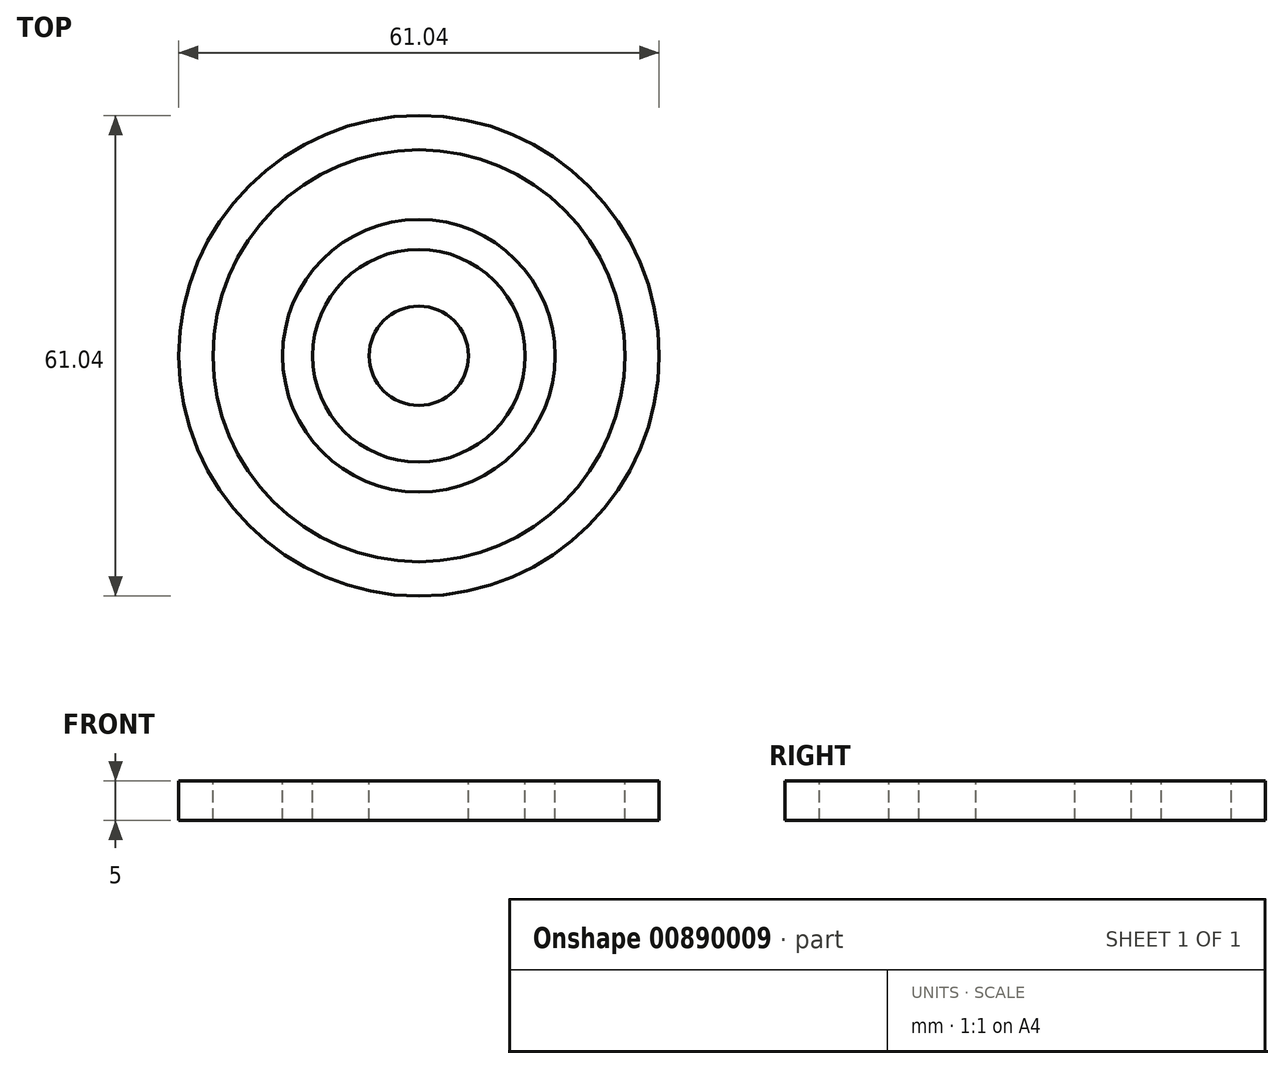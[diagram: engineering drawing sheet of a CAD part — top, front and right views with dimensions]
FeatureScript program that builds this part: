
annotation { "Feature Type Name" : "Feature", "Feature Type Description" : "" }
export const myFeature = defineFeature(function(context is Context, id is Id, definition is map)
    precondition{}
    {
        {
            var Q0;
            Q0=qCreatedBy(makeId("Top.planeOp"),FACE);
            var sketch = newSketch(context, id + "F0", { "sketchPlane" : qUnion([Q0])});
            skCircle(sketch, "E0", {"center": v(0, 0) * mm, "radius": 30.52 * mm});
            skCircle(sketch, "E1", {"center": v(0, 0) * mm, "radius": 26.17 * mm});
            skCircle(sketch, "E2", {"center": v(0, 0) * mm, "radius": 22.3 * mm});
            skCircle(sketch, "E3", {"center": v(0, 0) * mm, "radius": 17.3 * mm});
            skCircle(sketch, "E4", {"center": v(0, 0) * mm, "radius": 13.5 * mm});
            skCircle(sketch, "E5", {"center": v(0, 0) * mm, "radius": 9.48 * mm});
            skCircle(sketch, "E6", {"center": v(0, 0) * mm, "radius": 6.3 * mm});
            skSolve(sketch);
        }
        {
            var Q0;
            Q0=sQuery(id+"F0.wireOp",EDGE,"E0");
            var Q1;
            Q1=sQuery(id+"F0.wireOp",EDGE,"E1");
            var Q2;
            Q2=sQuery(id+"F0.wireOp",EDGE,"E3");
            var Q3;
            Q3=sQuery(id+"F0.wireOp",EDGE,"E4");
            var Q4;
            Q4=sQuery(id+"F0.wireOp",EDGE,"E6");
            extrude(context, id + "F1", {"bodyType" : ToolBodyType.SURFACE, "surfaceEntities" : qUnion([Q0, Q1, Q2, Q3, Q4]), "depth" : 5 * mm, "offsetDistance" : 25.4 * mm});
        }
    });
